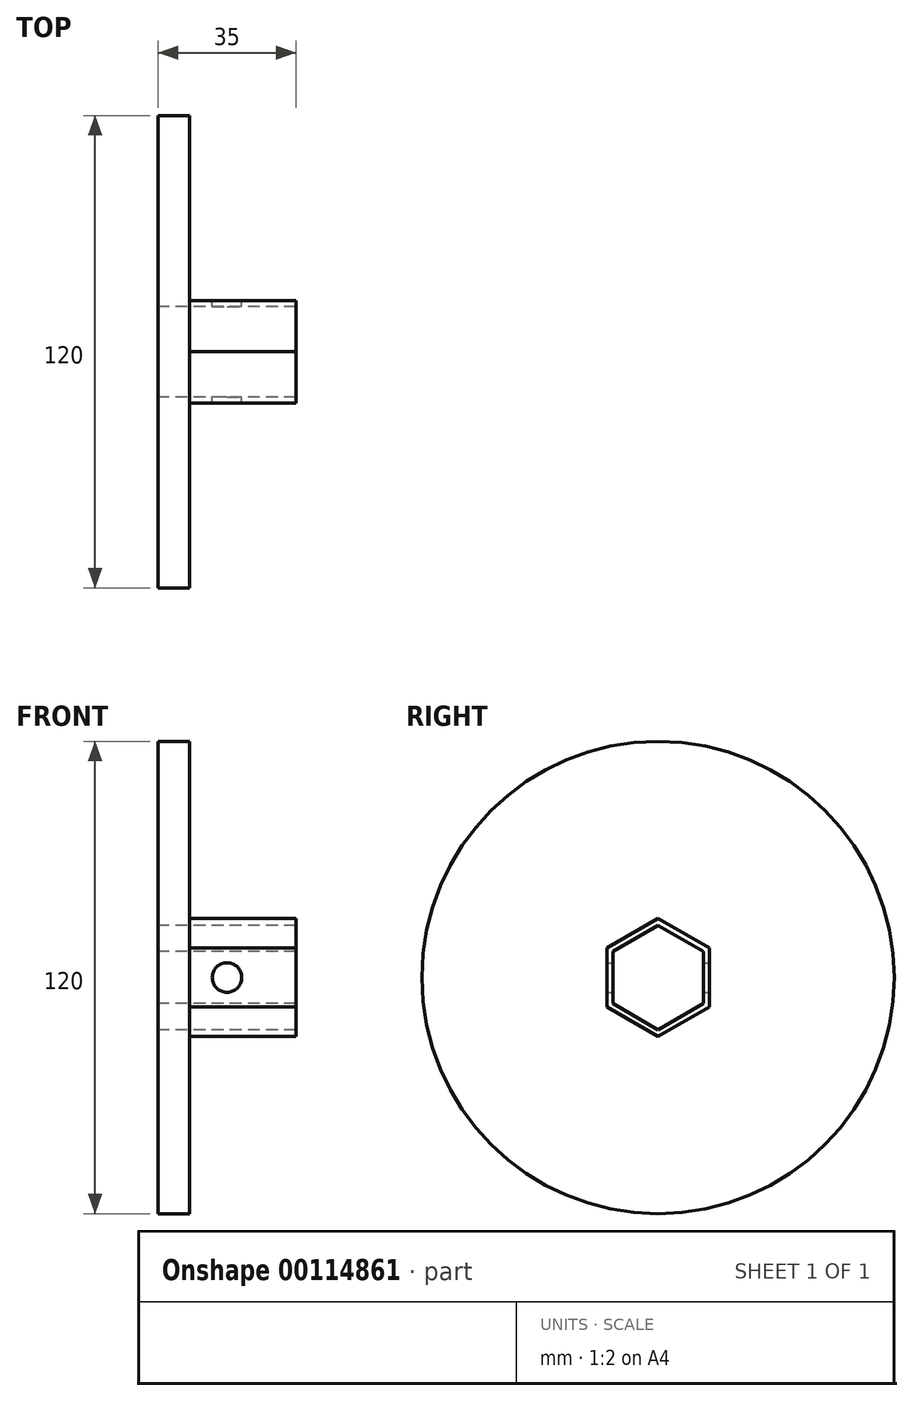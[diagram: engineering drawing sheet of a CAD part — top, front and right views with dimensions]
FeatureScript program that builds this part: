
annotation { "Feature Type Name" : "Feature", "Feature Type Description" : "" }
export const myFeature = defineFeature(function(context is Context, id is Id, definition is map)
    precondition{}
    {
        {
            var Q0;
            Q0=qCreatedBy(makeId("Right.planeOp"),FACE);
            var sketch = newSketch(context, id + "F0", { "sketchPlane" : qUnion([Q0])});
            skCircle(sketch, "E0", {"center": v(0, 0) * mm, "radius": 60 * mm});
            skCircle(sketch, "E1.cCircle", {"center": v(0, 0) * mm, "radius": 11.5 * mm, "construction": true});
            skLineSegment(sketch, "E1.0", {"start": v(11.5, 6.64) * mm, "end": v(11.5, -6.64) * mm});
            skLineSegment(sketch, "E1.1", {"start": v(11.5, -6.64) * mm, "end": v(0, -13.28) * mm});
            skLineSegment(sketch, "E1.2", {"start": v(0, -13.28) * mm, "end": v(-11.5, -6.64) * mm});
            skLineSegment(sketch, "E1.3", {"start": v(-11.5, -6.64) * mm, "end": v(-11.5, 6.64) * mm});
            skLineSegment(sketch, "E1.4", {"start": v(-11.5, 6.64) * mm, "end": v(0, 13.28) * mm});
            skLineSegment(sketch, "E1.5", {"start": v(0, 13.28) * mm, "end": v(11.5, 6.64) * mm});
            skPoint(sketch, "E1.0.midPoint", {"position": v(11.5, 0) * mm});
            skSolve(sketch);
        }
        {
            var Q0;
            Q0=makeQuery(id+"F0.imprint","IMPRINT",FACE,{"disambiguationData":[TD([[makeQuery(id+"F0.imprint","IMPRINT",EDGE,{"derivedFrom":sQuery(id+"F0.wireOp",EDGE,"E0")}),1.0]])]});
            extrude(context, id + "F1", {"entities" : qUnion([Q0]), "depth" : 35 * mm});
        }
        {
            var Q0;
            Q0=makeQuery(id+"F1.opExtrude","CAP_FACE",FACE,{"disambiguationData":[OSD([sQuery(id+"F0.wireOp",EDGE,"E0"),sQuery(id+"F0.wireOp",EDGE,"7abc851a-74dc-4893-8c03-ffff46612325.0"),sQuery(id+"F0.wireOp",EDGE,"7abc851a-74dc-4893-8c03-ffff46612325.1"),sQuery(id+"F0.wireOp",EDGE,"7abc851a-74dc-4893-8c03-ffff46612325.2"),sQuery(id+"F0.wireOp",EDGE,"7abc851a-74dc-4893-8c03-ffff46612325.3"),sQuery(id+"F0.wireOp",EDGE,"7abc851a-74dc-4893-8c03-ffff46612325.4"),sQuery(id+"F0.wireOp",EDGE,"7abc851a-74dc-4893-8c03-ffff46612325.5")])],"isStart":false});
            var sketch = newSketch(context, id + "F2", { "sketchPlane" : qUnion([Q0])});
            skCircle(sketch, "E2.cCircle", {"center": v(0, 0) * mm, "radius": 13 * mm, "construction": true});
            skLineSegment(sketch, "E2.0", {"start": v(13, 7.5) * mm, "end": v(13, -7.5) * mm});
            skLineSegment(sketch, "E2.1", {"start": v(13, -7.5) * mm, "end": v(0, -15.01) * mm});
            skLineSegment(sketch, "E2.2", {"start": v(0, -15.01) * mm, "end": v(-13, -7.5) * mm});
            skLineSegment(sketch, "E2.3", {"start": v(-13, -7.5) * mm, "end": v(-13, 7.5) * mm});
            skLineSegment(sketch, "E2.4", {"start": v(-13, 7.5) * mm, "end": v(0, 15.01) * mm});
            skLineSegment(sketch, "E2.5", {"start": v(0, 15.01) * mm, "end": v(13, 7.5) * mm});
            skPoint(sketch, "E2.0.midPoint", {"position": v(13, 0) * mm});
            skSolve(sketch);
        }
        {
            var Q0;
            Q0=makeQuery(id+"F2.imprint","IMPRINT",FACE,{"disambiguationData":[TD([[makeQuery(id+"F2.imprint","IMPRINT",EDGE,{"derivedFrom":sQuery(id+"F2.wireOp",EDGE,"E2.0")}),1.0]])]});
            extrude(context, id + "F3", {"entities" : qUnion([Q0]), "operationType" : NewBodyOperationType.REMOVE, "oppositeDirection" : true, "depth" : 27 * mm});
        }
        {
            var Q0;
            Q0=makeQuery(id+"F3.boolean.opBoolean","COPY",FACE,{"derivedFrom":makeQuery(id+"F3.opExtrude","SWEPT_FACE",FACE,{"disambiguationData":[OSD([sQuery(id+"F2.wireOp",EDGE,"E2.0")])]})});
            var sketch = newSketch(context, id + "F4", { "sketchPlane" : qUnion([Q0])});
            skPoint(sketch, "E3.endSnap0", {"position": v(-35, 0) * mm});
            skCircle(sketch, "E4", {"center": v(-17.5, 0) * mm, "radius": 3.75 * mm});
            skSolve(sketch);
        }
        {
            var Q0;
            Q0=makeQuery(id+"F4.imprint","IMPRINT",FACE,{"disambiguationData":[TD([[makeQuery(id+"F4.imprint","IMPRINT",EDGE,{"derivedFrom":sQuery(id+"F4.wireOp",EDGE,"E4")}),1.0]])]});
            extrude(context, id + "F5", {"entities" : qUnion([Q0]), "operationType" : NewBodyOperationType.REMOVE, "oppositeDirection" : true, "depth" : 44.75 * mm});
        }
    });
